# Revit family: BI-40
name_source: partatom
category: Generic Models
revit_build: Autodesk Revit LT 2016 (Build: 20161004_0715(x64)
units: mm (PartAtom-declared; Revit-internal decimal feet)

## family parameters
Always vertical = Yes
Can host rebar = No
Cut with Voids When Loaded = No
Part Type = Normal
Room Calculation Point = No
Round Connector Dimension = Use Diameter
Shared = No
Work Plane-Based = No

## types (2) — shared parameters
K = 3 3/8"
L = 5 3/4"
Manufacturer = REVERSOMATIC
URL = http://www.reversomatic.com

## per-type parameters (varying)
| type | A | AB | B | BLADE | C | D | E | F | G | H | HOUSING | I | J | MOTOR | Model | RPM | SP/CFM |
| GPB2-130  REVERSO DESIGN | 8 7/8" | 13 3/4" | 4 7/8" | AA-326-128 | 9 3/4" | 4 3/8" | 7 1/2" | 6 3/4" | 9" | 4 1/8" | REVERSO | 37" | 5" | 302-5929 | GPB2-130 | 1500 | .00/127  .05/118  .10/104  .15/88  .20/72 |
| GPB2-130 BF-00 | 75" | 83" | 8" |  | 40" | 24" | 45" | 31 1/4" | 41" | 43 1/2" |  | 78" | 70" |  | BI-40 |  |  |

## geometry (parser evidence)
native form markers: Sweep x2
no freeform markers — native parametric forms only
